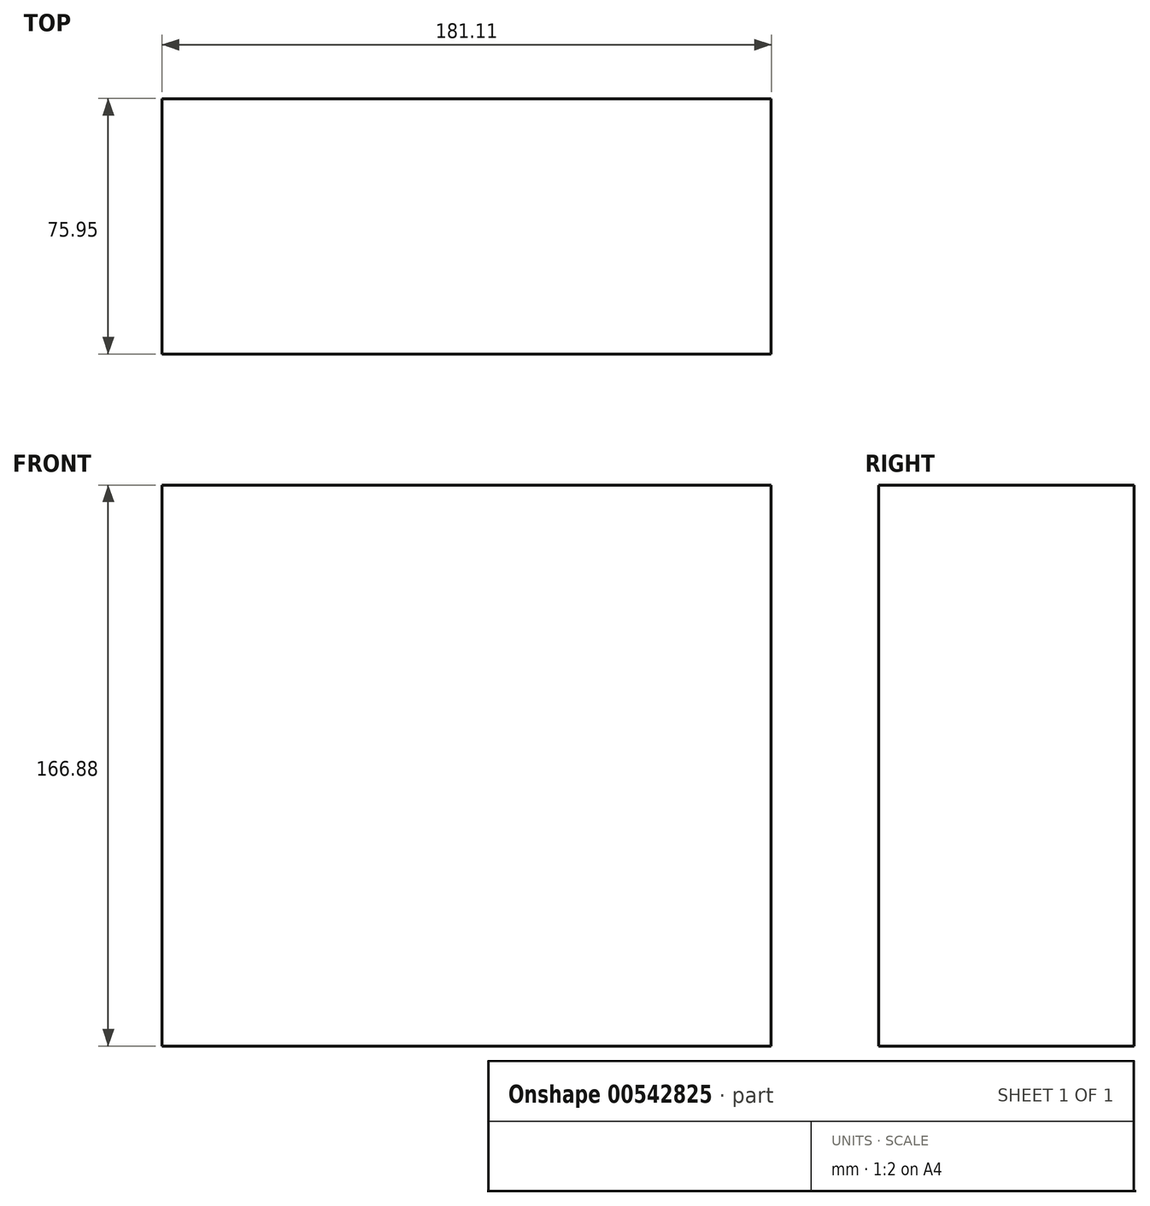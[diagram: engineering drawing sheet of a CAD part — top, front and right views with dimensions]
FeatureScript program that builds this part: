
annotation { "Feature Type Name" : "Feature", "Feature Type Description" : "" }
export const myFeature = defineFeature(function(context is Context, id is Id, definition is map)
    precondition{}
    {
        {
            var Q0;
            Q0=qCreatedBy(makeId("Top.planeOp"),FACE);
            var sketch = newSketch(context, id + "F0", { "sketchPlane" : qUnion([Q0])});
            skLineSegment(sketch, "E0.bottom", {"start": v(-47.35, 26.94) * mm, "end": v(133.76, 26.94) * mm});
            skLineSegment(sketch, "E0.top", {"start": v(-47.35, -49) * mm, "end": v(133.76, -49) * mm});
            skLineSegment(sketch, "E0.left", {"start": v(-47.35, 26.94) * mm, "end": v(-47.35, -49) * mm});
            skLineSegment(sketch, "E0.right", {"start": v(133.76, 26.94) * mm, "end": v(133.76, -49) * mm});
            skSolve(sketch);
        }
        {
            var Q0;
            Q0=makeQuery(id+"F0.imprint","IMPRINT",FACE,{"disambiguationData":[TD([[makeQuery(id+"F0.imprint","IMPRINT",EDGE,{"derivedFrom":sQuery(id+"F0.wireOp",EDGE,"E0.bottom")}),-1.0]])]});
            extrude(context, id + "F1", {"entities" : qUnion([Q0]), "depth" : 166.88 * mm});
        }
    });
